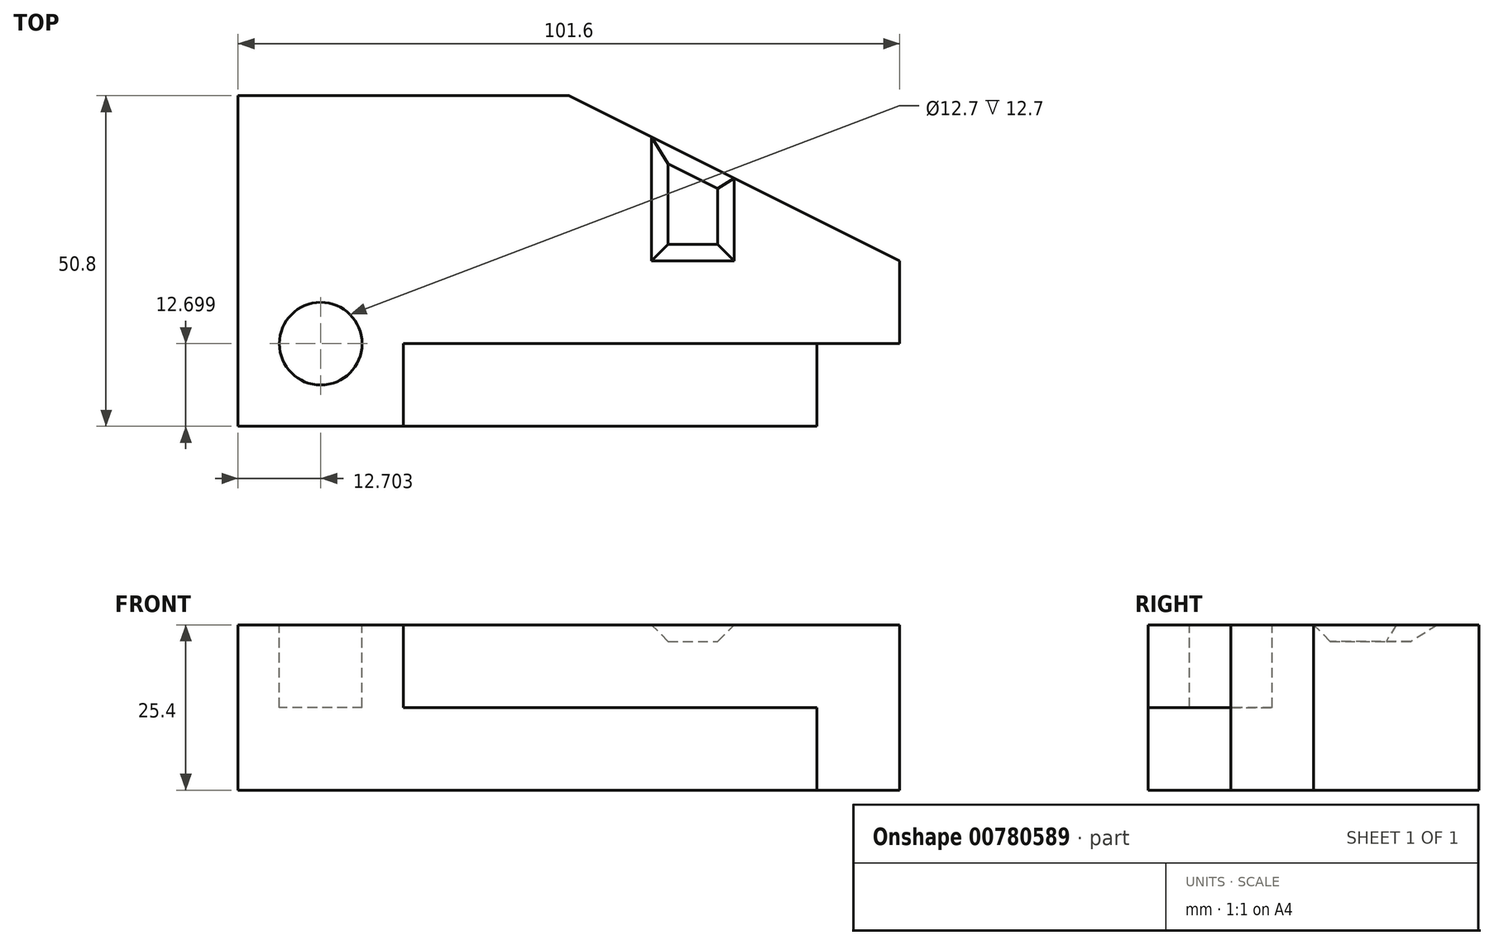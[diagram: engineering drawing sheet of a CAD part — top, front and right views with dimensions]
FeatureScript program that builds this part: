
annotation { "Feature Type Name" : "Feature", "Feature Type Description" : "" }
export const myFeature = defineFeature(function(context is Context, id is Id, definition is map)
    precondition{}
    {
        {
            var Q0;
            Q0=qCreatedBy(makeId("Top.planeOp"),FACE);
            var sketch = newSketch(context, id + "F0", { "sketchPlane" : qUnion([Q0])});
            skLineSegment(sketch, "E0", {"start": v(-40.76, -10.51) * mm, "end": v(-40.76, 40.29) * mm});
            skLineSegment(sketch, "E1", {"start": v(-40.76, 40.29) * mm, "end": v(10.04, 40.29) * mm});
            skLineSegment(sketch, "E2", {"start": v(-40.76, -10.51) * mm, "end": v(48.14, -10.51) * mm});
            skLineSegment(sketch, "E3", {"start": v(48.14, -10.51) * mm, "end": v(48.14, 2.19) * mm});
            skLineSegment(sketch, "E4", {"start": v(48.14, 2.19) * mm, "end": v(60.84, 2.19) * mm});
            skLineSegment(sketch, "E5", {"start": v(60.84, 2.19) * mm, "end": v(60.84, 14.89) * mm});
            skLineSegment(sketch, "E6", {"start": v(60.84, 14.89) * mm, "end": v(10.04, 40.29) * mm});
            skSolve(sketch);
        }
        {
            var Q0;
            Q0 = qSketchRegion(id + "F0", true);
            extrude(context, id + "F1", {"entities" : qUnion([Q0]), "depth" : 12.7 * mm, "offsetDistance" : 25.4 * mm});
        }
        {
            var Q0;
            Q0=makeQuery(id+"F1.opExtrude","CAP_FACE",FACE,{"disambiguationData":[OSD([sQuery(id+"F0.wireOp",EDGE,"E0"),sQuery(id+"F0.wireOp",EDGE,"E1"),sQuery(id+"F0.wireOp",EDGE,"E2"),sQuery(id+"F0.wireOp",EDGE,"E3"),sQuery(id+"F0.wireOp",EDGE,"E4"),sQuery(id+"F0.wireOp",EDGE,"E5"),sQuery(id+"F0.wireOp",EDGE,"E6")])],"isStart":false});
            var sketch = newSketch(context, id + "F2", { "sketchPlane" : qUnion([Q0])});
            skLineSegment(sketch, "E7", {"start": v(-40.76, -10.51) * mm, "end": v(-15.36, -10.51) * mm});
            skLineSegment(sketch, "E8", {"start": v(-15.36, -10.51) * mm, "end": v(-15.36, 2.19) * mm});
            skLineSegment(sketch, "E9", {"start": v(48.14, 2.19) * mm, "end": v(-15.36, 2.19) * mm});
            skSolve(sketch);
        }
        {
            var Q0;
            Q0=makeQuery(id+"F2.imprint","IMPRINT",FACE,{"disambiguationData":[TD([[makeQuery(id+"F2.imprint","IMPRINT",EDGE,{"derivedFrom":sQuery(id+"F2.wireOp",EDGE,"E7")}),1.0]])]});
            extrude(context, id + "F3", {"entities" : qUnion([Q0]), "operationType" : NewBodyOperationType.ADD, "depth" : 12.7 * mm, "offsetDistance" : 25.4 * mm});
        }
        {
            var Q0;
            Q0=makeQuery(id+"F3.opExtrude","CAP_FACE",FACE,{"disambiguationData":[OSD([sQuery(id+"F0.wireOp",EDGE,"E0"),sQuery(id+"F0.wireOp",EDGE,"E1"),sQuery(id+"F0.wireOp",EDGE,"E4"),sQuery(id+"F0.wireOp",EDGE,"E5"),sQuery(id+"F0.wireOp",EDGE,"E6"),sQuery(id+"F2.wireOp",EDGE,"E7"),sQuery(id+"F2.wireOp",EDGE,"E8"),sQuery(id+"F2.wireOp",EDGE,"E9")])],"isStart":false});
            var sketch = newSketch(context, id + "F4", { "sketchPlane" : qUnion([Q0])});
            skLineSegment(sketch, "E10", {"start": v(-28.06, -10.51) * mm, "end": v(-28.06, 40.29) * mm, "construction": true});
            skLineSegment(sketch, "E11", {"start": v(-15.36, 2.19) * mm, "end": v(-40.76, 2.19) * mm, "construction": true});
            skCircle(sketch, "E12", {"center": v(-28.06, 2.19) * mm, "radius": 6.35 * mm});
            skSolve(sketch);
        }
        {
            var Q0;
            Q0 = qSketchRegion(id + "F4", true);
            extrude(context, id + "F5", {"entities" : qUnion([Q0]), "operationType" : NewBodyOperationType.REMOVE, "oppositeDirection" : true, "depth" : 12.7 * mm, "offsetDistance" : 25.4 * mm});
        }
        {
            var Q0;
            Q0=makeQuery(id+"F3.opExtrude","CAP_FACE",FACE,{"disambiguationData":[OSD([sQuery(id+"F0.wireOp",EDGE,"E0"),sQuery(id+"F0.wireOp",EDGE,"E1"),sQuery(id+"F0.wireOp",EDGE,"E4"),sQuery(id+"F0.wireOp",EDGE,"E5"),sQuery(id+"F0.wireOp",EDGE,"E6"),sQuery(id+"F2.wireOp",EDGE,"E7"),sQuery(id+"F2.wireOp",EDGE,"E8"),sQuery(id+"F2.wireOp",EDGE,"E9")])],"isStart":false});
            var sketch = newSketch(context, id + "F6", { "sketchPlane" : qUnion([Q0])});
            skLineSegment(sketch, "E13", {"start": v(60.84, 14.89) * mm, "end": v(22.74, 14.89) * mm});
            skLineSegment(sketch, "E14", {"start": v(22.74, 14.89) * mm, "end": v(22.74, 33.94) * mm});
            skLineSegment(sketch, "E15", {"start": v(35.44, 27.59) * mm, "end": v(35.44, 14.89) * mm});
            skLineSegment(sketch, "E16", {"start": v(22.74, 33.94) * mm, "end": v(35.44, 27.59) * mm});
            skSolve(sketch);
        }
        {
            var Q0;
            Q0 = qSketchRegion(id + "F6", true);
            extrude(context, id + "F7", {"entities" : qUnion([Q0]), "operationType" : NewBodyOperationType.REMOVE, "oppositeDirection" : true, "depth" : 2.54 * mm, "offsetDistance" : 25.4 * mm, "hasDraft" : true, "draftAngle" : 45 * degree, "draftPullDirection" : true});
        }
    });
